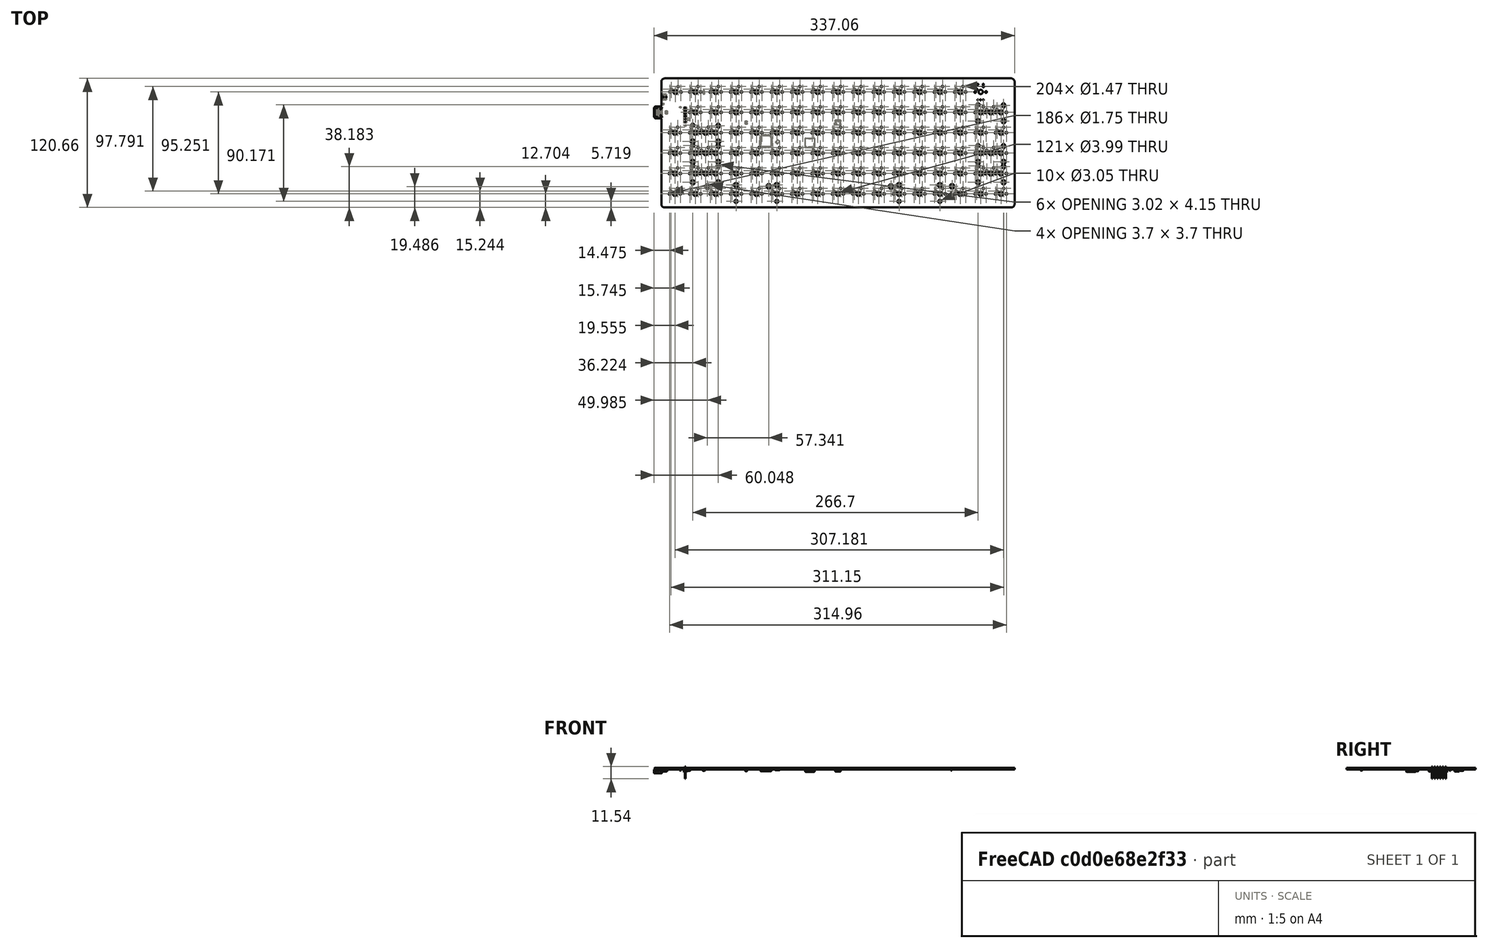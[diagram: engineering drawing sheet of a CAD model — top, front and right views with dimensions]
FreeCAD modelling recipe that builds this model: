
FCSTD DOCUMENT  (FreeCAD 0.19R24291 (Git))
Label: Orthonite87_001
License: All rights reserved
LicenseURL: http://en.wikipedia.org/wiki/All_rights_reserved
objects: App::Link×162, Part::Feature×18, App::Part×4, PartDesign::CoordinateSystem×1, Sketcher::SketchObject×1
note: 20 computed .brp shape members not serialized (recipe doc carries the construction recipe); baked Part::Feature solids carry a one-line shape summary decoded from their .brp

FEATURE [PartDesign::CoordinateSystem] Local_CS_e1db
  AttacherType = Attacher::AttachEngine3D
FEATURE [Part::Feature] Pcb_e1db
  Placement = pos=(-174.625,80.9625,0) rot=(0,0,1;0rad)
  shape: bbox 336.6 x 120.7 x 1.6 mm, 675 faces (baked)
FEATURE [Sketcher::SketchObject] PCB_Sketch_e1db
  FullyConstrained = false
  sketch-geometry (18):
    g0: LineSegment StartX=-168.275 StartY=33.3375 StartZ=0 EndX=-168.275 EndY=23.8125 EndZ=0
    g1: LineSegment StartX=-163.512 StartY=23.0188 StartZ=0 EndX=-162.719 EndY=23.0188 EndZ=0
    g2: LineSegment StartX=-163.512 StartY=34.1313 StartZ=0 EndX=-162.719 EndY=34.1313 EndZ=0
    g3: LineSegment StartX=-167.481 StartY=34.1313 StartZ=0 EndX=-163.512 EndY=34.1313 EndZ=0
    g4: LineSegment StartX=-163.512 StartY=23.0188 StartZ=0 EndX=-167.481 EndY=23.0188 EndZ=0
    g5: LineSegment StartX=-161.925 StartY=22.225 StartZ=0 EndX=-161.925 EndY=-57.15 EndZ=0
    g6: LineSegment StartX=-161.925 StartY=57.15 StartZ=0 EndX=-161.925 EndY=34.925 EndZ=0
    g7: LineSegment StartX=168.275 StartY=-57.15 StartZ=0 EndX=168.275 EndY=57.15 EndZ=0
    g8: LineSegment StartX=-158.75 StartY=-60.325 StartZ=0 EndX=165.1 EndY=-60.325 EndZ=0
    g9: LineSegment StartX=-158.75 StartY=60.325 StartZ=0 EndX=165.1 EndY=60.325 EndZ=0
    g10: ArcOfCircle CenterX=-167.481 CenterY=33.3375 CenterZ=0 NormalX=0 NormalY=0 NormalZ=1 AngleXU=0 Radius=0.79375 StartAngle=1.5708 EndAngle=3.14159
    g11: ArcOfCircle CenterX=-167.481 CenterY=23.8125 CenterZ=0 NormalX=0 NormalY=0 NormalZ=1 AngleXU=0 Radius=0.79375 StartAngle=3.14159 EndAngle=4.71239
    g12: ArcOfCircle CenterX=-162.719 CenterY=22.225 CenterZ=0 NormalX=0 NormalY=0 NormalZ=1 AngleXU=0 Radius=0.79375 StartAngle=0 EndAngle=1.5708
    g13: ArcOfCircle CenterX=-162.719 CenterY=34.925 CenterZ=0 NormalX=0 NormalY=0 NormalZ=1 AngleXU=0 Radius=0.79375 StartAngle=4.71239 EndAngle=6.28319
    g14: ArcOfCircle CenterX=165.1 CenterY=-57.15 CenterZ=0 NormalX=0 NormalY=0 NormalZ=1 AngleXU=0 Radius=3.175 StartAngle=4.71239 EndAngle=6.28319
    g15: ArcOfCircle CenterX=-158.75 CenterY=-57.15 CenterZ=0 NormalX=0 NormalY=0 NormalZ=1 AngleXU=0 Radius=3.175 StartAngle=3.14159 EndAngle=4.71239
    g16: ArcOfCircle CenterX=-158.75 CenterY=57.15 CenterZ=0 NormalX=0 NormalY=0 NormalZ=1 AngleXU=0 Radius=3.175 StartAngle=1.5708 EndAngle=3.14159
    g17: ArcOfCircle CenterX=165.1 CenterY=57.15 CenterZ=0 NormalX=0 NormalY=0 NormalZ=1 AngleXU=0 Radius=3.175 StartAngle=0 EndAngle=1.5708
FEATURE [Part::Feature] Shape  label="C37_C_0603_1608Metric_611CB56A"
  Placement = pos=(109.156,-46.4185,-1.6) rot=(0.707107,0.707107,0;3.14159rad)
  shape: bbox 0.8 x 1.6 x 0.8 mm, 28 faces (baked)
FEATURE [App::Link] C37_C_0603_1608Metric_611CB56A_ln_  label="C36_C_0603_1608Metric_611CB560"
  LinkPlacement = pos=(52.045,-46.6345,-1.6) rot=(0.707107,0.707107,0;3.14159rad)
  LinkedObject = -> Shape
  Placement = pos=(52.045,-46.6345,-1.6) rot=(0.707107,0.707107,0;3.14159rad)
FEATURE [App::Link] C37_C_0603_1608Metric_611CB56A_ln_001  label="C35_C_0603_1608Metric_611CB556"
  LinkPlacement = pos=(-62.166,-46.2285,-1.6) rot=(0.707107,0.707107,0;3.14159rad)
  LinkedObject = -> Shape
  Placement = pos=(-62.166,-46.2285,-1.6) rot=(0.707107,0.707107,0;3.14159rad)
FEATURE [App::Link] C37_C_0603_1608Metric_611CB56A_ln_002  label="C34_C_0603_1608Metric_611CB54C"
  LinkPlacement = pos=(-119.507,-46.5455,-1.6) rot=(0.707107,0.707107,0;3.14159rad)
  LinkedObject = -> Shape
  Placement = pos=(-119.507,-46.5455,-1.6) rot=(0.707107,0.707107,0;3.14159rad)
FEATURE [App::Link] C37_C_0603_1608Metric_611CB56A_ln_003  label="C33_C_0603_1608Metric_611CB542"
  LinkPlacement = pos=(-99.568,-34.3535,-1.6) rot=(1,0,0;3.14159rad)
  LinkedObject = -> Shape
  Placement = pos=(-99.568,-34.3535,-1.6) rot=(1,0,0;3.14159rad)
FEATURE [App::Link] C37_C_0603_1608Metric_611CB56A_ln_004  label="C32_C_0603_1608Metric_611CB538"
  LinkPlacement = pos=(-42.545,-34.3535,-1.6) rot=(1,0,0;3.14159rad)
  LinkedObject = -> Shape
  Placement = pos=(-42.545,-34.3535,-1.6) rot=(1,0,0;3.14159rad)
FEATURE [App::Link] C37_C_0603_1608Metric_611CB56A_ln_005  label="C31_C_0603_1608Metric_611CB52E"
  LinkPlacement = pos=(5.08,-34.3535,-1.6) rot=(1,0,0;3.14159rad)
  LinkedObject = -> Shape
  Placement = pos=(5.08,-34.3535,-1.6) rot=(1,0,0;3.14159rad)
FEATURE [App::Link] C37_C_0603_1608Metric_611CB56A_ln_006  label="C30_C_0603_1608Metric_611CB524"
  LinkPlacement = pos=(71.704,-34.3785,-1.6) rot=(1,0,0;3.14159rad)
  LinkedObject = -> Shape
  Placement = pos=(71.704,-34.3785,-1.6) rot=(1,0,0;3.14159rad)
FEATURE [App::Link] C37_C_0603_1608Metric_611CB56A_ln_007  label="C29_C_0603_1608Metric_611CB51A"
  LinkPlacement = pos=(129.032,-34.3535,-1.6) rot=(1,0,0;3.14159rad)
  LinkedObject = -> Shape
  Placement = pos=(129.032,-34.3535,-1.6) rot=(1,0,0;3.14159rad)
FEATURE [App::Link] C37_C_0603_1608Metric_611CB56A_ln_008  label="C28_C_0603_1608Metric_611CB510"
  LinkPlacement = pos=(128.905,-15.3035,-1.6) rot=(1,0,0;3.14159rad)
  LinkedObject = -> Shape
  Placement = pos=(128.905,-15.3035,-1.6) rot=(1,0,0;3.14159rad)
FEATURE [App::Link] C37_C_0603_1608Metric_611CB56A_ln_009  label="C27_C_0603_1608Metric_611CB506"
  LinkPlacement = pos=(71.882,-15.3035,-1.6) rot=(1,0,0;3.14159rad)
  LinkedObject = -> Shape
  Placement = pos=(71.882,-15.3035,-1.6) rot=(1,0,0;3.14159rad)
FEATURE [App::Link] C37_C_0603_1608Metric_611CB56A_ln_010  label="C26_C_0603_1608Metric_611CB4FC"
  LinkPlacement = pos=(5.08,-15.3035,-1.6) rot=(1,0,0;3.14159rad)
  LinkedObject = -> Shape
  Placement = pos=(5.08,-15.3035,-1.6) rot=(1,0,0;3.14159rad)
FEATURE [App::Link] C37_C_0603_1608Metric_611CB56A_ln_011  label="C25_C_0603_1608Metric_611CB4F2"
  LinkPlacement = pos=(-42.545,-15.3035,-1.6) rot=(1,0,0;3.14159rad)
  LinkedObject = -> Shape
  Placement = pos=(-42.545,-15.3035,-1.6) rot=(1,0,0;3.14159rad)
FEATURE [App::Link] C37_C_0603_1608Metric_611CB56A_ln_012  label="C24_C_0603_1608Metric_611CB4E8"
  LinkPlacement = pos=(-99.695,-15.3035,-1.6) rot=(1,0,0;3.14159rad)
  LinkedObject = -> Shape
  Placement = pos=(-99.695,-15.3035,-1.6) rot=(1,0,0;3.14159rad)
FEATURE [App::Link] C37_C_0603_1608Metric_611CB56A_ln_013  label="C23_C_0603_1608Metric_611CB4DE"
  LinkPlacement = pos=(-99.695,3.7465,-1.6) rot=(1,0,0;3.14159rad)
  LinkedObject = -> Shape
  Placement = pos=(-99.695,3.7465,-1.6) rot=(1,0,0;3.14159rad)
FEATURE [App::Link] C37_C_0603_1608Metric_611CB56A_ln_014  label="C22_C_0603_1608Metric_611CB4D4"
  LinkPlacement = pos=(-42.545,3.7465,-1.6) rot=(1,0,0;3.14159rad)
  LinkedObject = -> Shape
  Placement = pos=(-42.545,3.7465,-1.6) rot=(1,0,0;3.14159rad)
FEATURE [App::Link] C37_C_0603_1608Metric_611CB56A_ln_015  label="C21_C_0603_1608Metric_611CB4CA"
  LinkPlacement = pos=(5.08,3.7465,-1.6) rot=(1,0,0;3.14159rad)
  LinkedObject = -> Shape
  Placement = pos=(5.08,3.7465,-1.6) rot=(1,0,0;3.14159rad)
FEATURE [App::Link] C37_C_0603_1608Metric_611CB56A_ln_016  label="C20_C_0603_1608Metric_611CB4C0"
  LinkPlacement = pos=(71.755,3.7465,-1.6) rot=(1,0,0;3.14159rad)
  LinkedObject = -> Shape
  Placement = pos=(71.755,3.7465,-1.6) rot=(1,0,0;3.14159rad)
FEATURE [App::Link] C37_C_0603_1608Metric_611CB56A_ln_017  label="C19_C_0603_1608Metric_611CB4B6"
  LinkPlacement = pos=(128.778,3.7465,-1.6) rot=(1,0,0;3.14159rad)
  LinkedObject = -> Shape
  Placement = pos=(128.778,3.7465,-1.6) rot=(1,0,0;3.14159rad)
FEATURE [App::Link] C37_C_0603_1608Metric_611CB56A_ln_018  label="C18_C_0603_1608Metric_611CB4AC"
  LinkPlacement = pos=(128.905,22.7965,-1.6) rot=(1,0,0;3.14159rad)
  LinkedObject = -> Shape
  Placement = pos=(128.905,22.7965,-1.6) rot=(1,0,0;3.14159rad)
FEATURE [App::Link] C37_C_0603_1608Metric_611CB56A_ln_019  label="C17_C_0603_1608Metric_611CB4A2"
  LinkPlacement = pos=(71.628,22.7965,-1.6) rot=(1,0,0;3.14159rad)
  LinkedObject = -> Shape
  Placement = pos=(71.628,22.7965,-1.6) rot=(1,0,0;3.14159rad)
FEATURE [App::Link] C37_C_0603_1608Metric_611CB56A_ln_020  label="C16_C_0603_1608Metric_611CB498"
  LinkPlacement = pos=(5.08,22.7965,-1.6) rot=(1,0,0;3.14159rad)
  LinkedObject = -> Shape
  Placement = pos=(5.08,22.7965,-1.6) rot=(1,0,0;3.14159rad)
FEATURE [App::Link] C37_C_0603_1608Metric_611CB56A_ln_021  label="C15_C_0603_1608Metric_611CB48E"
  LinkPlacement = pos=(-42.672,22.7965,-1.6) rot=(1,0,0;3.14159rad)
  LinkedObject = -> Shape
  Placement = pos=(-42.672,22.7965,-1.6) rot=(1,0,0;3.14159rad)
FEATURE [App::Link] C37_C_0603_1608Metric_611CB56A_ln_022  label="C14_C_0603_1608Metric_611CB484"
  LinkPlacement = pos=(-99.695,22.9235,-1.6) rot=(1,0,0;3.14159rad)
  LinkedObject = -> Shape
  Placement = pos=(-99.695,22.9235,-1.6) rot=(1,0,0;3.14159rad)
FEATURE [App::Link] C37_C_0603_1608Metric_611CB56A_ln_023  label="C13_C_0603_1608Metric_611CB47A"
  LinkPlacement = pos=(-139.231,17.7483,-1.6) rot=(0,1,0;3.14159rad)
  LinkedObject = -> Shape
  Placement = pos=(-139.231,17.7483,-1.6) rot=(0,1,0;3.14159rad)
FEATURE [App::Link] C37_C_0603_1608Metric_611CB56A_ln_024  label="C12_C_0603_1608Metric_611CB470"
  LinkPlacement = pos=(-134.144,21.4313,-1.6) rot=(-0.707107,0.707107,0;3.14159rad)
  LinkedObject = -> Shape
  Placement = pos=(-134.144,21.4313,-1.6) rot=(-0.707107,0.707107,0;3.14159rad)
FEATURE [App::Link] C37_C_0603_1608Metric_611CB56A_ln_025  label="C11_C_0603_1608Metric_611CB466"
  LinkPlacement = pos=(-51.054,4.7625,-1.6) rot=(1,0,0;3.14159rad)
  LinkedObject = -> Shape
  Placement = pos=(-51.054,4.7625,-1.6) rot=(1,0,0;3.14159rad)
FEATURE [App::Link] C37_C_0603_1608Metric_611CB56A_ln_026  label="C10_C_0603_1608Metric_611CB45C"
  LinkPlacement = pos=(-50.165,-1.0795,-1.6) rot=(1,0,0;3.14159rad)
  LinkedObject = -> Shape
  Placement = pos=(-50.165,-1.0795,-1.6) rot=(1,0,0;3.14159rad)
FEATURE [App::Link] C37_C_0603_1608Metric_611CB56A_ln_027  label="C9_C_0603_1608Metric_611CB452"
  LinkPlacement = pos=(-79.375,19.05,-1.6) rot=(-0.707107,0.707107,0;3.14159rad)
  LinkedObject = -> Shape
  Placement = pos=(-79.375,19.05,-1.6) rot=(-0.707107,0.707107,0;3.14159rad)
FEATURE [App::Link] C37_C_0603_1608Metric_611CB56A_ln_028  label="C8_C_0603_1608Metric_611CB448"
  LinkPlacement = pos=(-85.725,19.05,-1.6) rot=(-0.707107,0.707107,0;3.14159rad)
  LinkedObject = -> Shape
  Placement = pos=(-85.725,19.05,-1.6) rot=(-0.707107,0.707107,0;3.14159rad)
FEATURE [App::Link] C37_C_0603_1608Metric_611CB56A_ln_029  label="C7_C_0603_1608Metric_611CB43E"
  LinkPlacement = pos=(-146.844,34.1313,-1.6) rot=(-0.707107,0.707107,0;3.14159rad)
  LinkedObject = -> Shape
  Placement = pos=(-146.844,34.1313,-1.6) rot=(-0.707107,0.707107,0;3.14159rad)
FEATURE [App::Link] C37_C_0603_1608Metric_611CB56A_ln_030  label="C6_C_0603_1608Metric_611CB434"
  LinkPlacement = pos=(-61.722,-8.1915,-1.6) rot=(0.707107,0.707107,0;3.14159rad)
  LinkedObject = -> Shape
  Placement = pos=(-61.722,-8.1915,-1.6) rot=(0.707107,0.707107,0;3.14159rad)
FEATURE [App::Link] C37_C_0603_1608Metric_611CB56A_ln_031  label="C5_C_0603_1608Metric_611CB42A"
  LinkPlacement = pos=(-55.88,-3.6195,-1.6) rot=(0.707107,0.707107,0;3.14159rad)
  LinkedObject = -> Shape
  Placement = pos=(-55.88,-3.6195,-1.6) rot=(0.707107,0.707107,0;3.14159rad)
FEATURE [App::Link] C37_C_0603_1608Metric_611CB56A_ln_032  label="C4_C_0603_1608Metric_611CB420"
  LinkPlacement = pos=(-65.532,-8.0645,-1.6) rot=(0.707107,0.707107,0;3.14159rad)
  LinkedObject = -> Shape
  Placement = pos=(-65.532,-8.0645,-1.6) rot=(0.707107,0.707107,0;3.14159rad)
FEATURE [App::Link] C37_C_0603_1608Metric_611CB56A_ln_033  label="C3_C_0603_1608Metric_611CB416"
  LinkPlacement = pos=(-73.279,5.0165,-1.6) rot=(1,0,0;3.14159rad)
  LinkedObject = -> Shape
  Placement = pos=(-73.279,5.0165,-1.6) rot=(1,0,0;3.14159rad)
FEATURE [App::Link] C37_C_0603_1608Metric_611CB56A_ln_034  label="C2_C_0603_1608Metric_611CB40C"
  LinkPlacement = pos=(-62.23,10.8585,-1.6) rot=(-0.707107,0.707107,0;3.14159rad)
  LinkedObject = -> Shape
  Placement = pos=(-62.23,10.8585,-1.6) rot=(-0.707107,0.707107,0;3.14159rad)
FEATURE [App::Link] C37_C_0603_1608Metric_611CB56A_ln_035  label="C1_C_0603_1608Metric_611CB402"
  LinkPlacement = pos=(-75.819,4.1275,-1.6) rot=(-0.707107,0.707107,0;3.14159rad)
  LinkedObject = -> Shape
  Placement = pos=(-75.819,4.1275,-1.6) rot=(-0.707107,0.707107,0;3.14159rad)
FEATURE [Part::Feature] Shape001  label="D_2_D_SOD_123_611CB7E4"
  Placement = pos=(-122.174,47.3075,-1.6) rot=(0.707107,0.707107,0;3.14159rad)
  shape: bbox 1.6 x 3.8 x 1.25 mm, 67 faces (baked)
FEATURE [App::Link] D_2_D_SOD_123_611CB7E4_ln_  label="D_1_2_D_SOD_123_611CB7D3"
  LinkPlacement = pos=(-141.224,47.3085,-1.6) rot=(0.707107,0.707107,0;3.14159rad)
  LinkedObject = -> Shape001
  Placement = pos=(-141.224,47.3085,-1.6) rot=(0.707107,0.707107,0;3.14159rad)
FEATURE [App::Link] D_2_D_SOD_123_611CB7E4_ln_001  label="D_100_2_D_SOD_123_611CBE66"
  LinkPlacement = pos=(147.637,-47.2435,-1.6) rot=(0.707107,0.707107,0;3.14159rad)
  LinkedObject = -> Shape001
  Placement = pos=(147.637,-47.2435,-1.6) rot=(0.707107,0.707107,0;3.14159rad)
FEATURE [App::Link] D_2_D_SOD_123_611CB7E4_ln_002  label="D_99_2_D_SOD_123_611CBE55"
  LinkPlacement = pos=(144.463,-47.2435,-1.6) rot=(0.707107,0.707107,0;3.14159rad)
  LinkedObject = -> Shape001
  Placement = pos=(144.463,-47.2435,-1.6) rot=(0.707107,0.707107,0;3.14159rad)
FEATURE [App::Link] D_2_D_SOD_123_611CB7E4_ln_003  label="D_98_2_D_SOD_123_611CBE44"
  LinkPlacement = pos=(125.476,-47.2435,-1.6) rot=(0.707107,0.707107,0;3.14159rad)
  LinkedObject = -> Shape001
  Placement = pos=(125.476,-47.2435,-1.6) rot=(0.707107,0.707107,0;3.14159rad)
FEATURE [App::Link] D_2_D_SOD_123_611CB7E4_ln_004  label="D_97_2_D_SOD_123_611CBE33"
  LinkPlacement = pos=(106.363,-47.2435,-1.6) rot=(0.707107,0.707107,0;3.14159rad)
  LinkedObject = -> Shape001
  Placement = pos=(106.363,-47.2435,-1.6) rot=(0.707107,0.707107,0;3.14159rad)
FEATURE [App::Link] D_2_D_SOD_123_611CB7E4_ln_005  label="D_96_2_D_SOD_123_611CBE22"
  LinkPlacement = pos=(87.313,-47.2435,-1.6) rot=(0.707107,0.707107,0;3.14159rad)
  LinkedObject = -> Shape001
  Placement = pos=(87.313,-47.2435,-1.6) rot=(0.707107,0.707107,0;3.14159rad)
FEATURE [App::Link] D_2_D_SOD_123_611CB7E4_ln_006  label="D_95_2_D_SOD_123_611CBE11"
  LinkPlacement = pos=(68.326,-47.2435,-1.6) rot=(0.707107,0.707107,0;3.14159rad)
  LinkedObject = -> Shape001
  Placement = pos=(68.326,-47.2435,-1.6) rot=(0.707107,0.707107,0;3.14159rad)
FEATURE [App::Link] D_2_D_SOD_123_611CB7E4_ln_007  label="D_94_2_D_SOD_123_611CBE00"
  LinkPlacement = pos=(49.213,-47.2435,-1.6) rot=(0.707107,0.707107,0;3.14159rad)
  LinkedObject = -> Shape001
  Placement = pos=(49.213,-47.2435,-1.6) rot=(0.707107,0.707107,0;3.14159rad)
FEATURE [App::Link] D_2_D_SOD_123_611CB7E4_ln_008  label="D_93_2_D_SOD_123_611CBDEF"
  LinkPlacement = pos=(30.163,-47.2435,-1.6) rot=(0.707107,0.707107,0;3.14159rad)
  LinkedObject = -> Shape001
  Placement = pos=(30.163,-47.2435,-1.6) rot=(0.707107,0.707107,0;3.14159rad)
FEATURE [App::Link] D_2_D_SOD_123_611CB7E4_ln_009  label="D_92_2_D_SOD_123_611CBDDE"
  LinkPlacement = pos=(11.176,-47.2435,-1.6) rot=(0.707107,0.707107,0;3.14159rad)
  LinkedObject = -> Shape001
  Placement = pos=(11.176,-47.2435,-1.6) rot=(0.707107,0.707107,0;3.14159rad)
FEATURE [App::Link] D_2_D_SOD_123_611CB7E4_ln_010  label="D_91_2_D_SOD_123_611CBDCD"
  LinkPlacement = pos=(-7.874,-47.2435,-1.6) rot=(0.707107,0.707107,0;3.14159rad)
  LinkedObject = -> Shape001
  Placement = pos=(-7.874,-47.2435,-1.6) rot=(0.707107,0.707107,0;3.14159rad)
FEATURE [App::Link] D_2_D_SOD_123_611CB7E4_ln_011  label="D_90_2_D_SOD_123_611CBDBC"
  LinkPlacement = pos=(-26.987,-47.3075,-1.6) rot=(0.707107,0.707107,0;3.14159rad)
  LinkedObject = -> Shape001
  Placement = pos=(-26.987,-47.3075,-1.6) rot=(0.707107,0.707107,0;3.14159rad)
FEATURE [App::Link] D_2_D_SOD_123_611CB7E4_ln_012  label="D_89_2_D_SOD_123_611CBDAB"
  LinkPlacement = pos=(-46.037,-47.2435,-1.6) rot=(0.707107,0.707107,0;3.14159rad)
  LinkedObject = -> Shape001
  Placement = pos=(-46.037,-47.2435,-1.6) rot=(0.707107,0.707107,0;3.14159rad)
FEATURE [App::Link] D_2_D_SOD_123_611CB7E4_ln_013  label="D_88_2_D_SOD_123_611CBD9A"
  LinkPlacement = pos=(-65.087,-47.2435,-1.6) rot=(0.707107,0.707107,0;3.14159rad)
  LinkedObject = -> Shape001
  Placement = pos=(-65.087,-47.2435,-1.6) rot=(0.707107,0.707107,0;3.14159rad)
FEATURE [App::Link] D_2_D_SOD_123_611CB7E4_ln_014  label="D_87_2_D_SOD_123_611CBD89"
  LinkPlacement = pos=(-84.1375,-47.3075,-1.6) rot=(0.707107,0.707107,0;3.14159rad)
  LinkedObject = -> Shape001
  Placement = pos=(-84.1375,-47.3075,-1.6) rot=(0.707107,0.707107,0;3.14159rad)
FEATURE [App::Link] D_2_D_SOD_123_611CB7E4_ln_015  label="D_86_2_D_SOD_123_611CBD78"
  LinkPlacement = pos=(-103.187,-47.2435,-1.6) rot=(0.707107,0.707107,0;3.14159rad)
  LinkedObject = -> Shape001
  Placement = pos=(-103.187,-47.2435,-1.6) rot=(0.707107,0.707107,0;3.14159rad)
FEATURE [App::Link] D_2_D_SOD_123_611CB7E4_ln_016  label="D_85_2_D_SOD_123_611CBD67"
  LinkPlacement = pos=(-122.237,-47.3075,-1.6) rot=(0.707107,0.707107,0;3.14159rad)
  LinkedObject = -> Shape001
  Placement = pos=(-122.237,-47.3075,-1.6) rot=(0.707107,0.707107,0;3.14159rad)
FEATURE [App::Link] D_2_D_SOD_123_611CB7E4_ln_017  label="D_84_2_D_SOD_123_611CBD56"
  LinkPlacement = pos=(-141.288,-47.3075,-1.6) rot=(0.707107,0.707107,0;3.14159rad)
  LinkedObject = -> Shape001
  Placement = pos=(-141.288,-47.3075,-1.6) rot=(0.707107,0.707107,0;3.14159rad)
FEATURE [App::Link] D_2_D_SOD_123_611CB7E4_ln_018  label="D_83_2_D_SOD_123_611CBD45"
  LinkPlacement = pos=(144.463,-21.4635,-1.6) rot=(0.707107,0.707107,0;3.14159rad)
  LinkedObject = -> Shape001
  Placement = pos=(144.463,-21.4635,-1.6) rot=(0.707107,0.707107,0;3.14159rad)
FEATURE [App::Link] D_2_D_SOD_123_611CB7E4_ln_019  label="D_82_2_D_SOD_123_611CBD34"
  LinkPlacement = pos=(128.587,-28.2575,-1.6) rot=(0.707107,0.707107,0;3.14159rad)
  LinkedObject = -> Shape001
  Placement = pos=(128.587,-28.2575,-1.6) rot=(0.707107,0.707107,0;3.14159rad)
FEATURE [App::Link] D_2_D_SOD_123_611CB7E4_ln_020  label="D_81_2_D_SOD_123_611CBD23"
  LinkPlacement = pos=(125.413,-28.2575,-1.6) rot=(0.707107,0.707107,0;3.14159rad)
  LinkedObject = -> Shape001
  Placement = pos=(125.413,-28.2575,-1.6) rot=(0.707107,0.707107,0;3.14159rad)
FEATURE [App::Link] D_2_D_SOD_123_611CB7E4_ln_021  label="D_80_2_D_SOD_123_611CBD12"
  LinkPlacement = pos=(106.363,-28.1935,-1.6) rot=(0.707107,0.707107,0;3.14159rad)
  LinkedObject = -> Shape001
  Placement = pos=(106.363,-28.1935,-1.6) rot=(0.707107,0.707107,0;3.14159rad)
FEATURE [App::Link] D_2_D_SOD_123_611CB7E4_ln_022  label="D_79_2_D_SOD_123_611CBD01"
  LinkPlacement = pos=(87.313,-28.1935,-1.6) rot=(0.707107,0.707107,0;3.14159rad)
  LinkedObject = -> Shape001
  Placement = pos=(87.313,-28.1935,-1.6) rot=(0.707107,0.707107,0;3.14159rad)
FEATURE [App::Link] D_2_D_SOD_123_611CB7E4_ln_023  label="D_78_2_D_SOD_123_611CBCF0"
  LinkPlacement = pos=(68.263,-28.1935,-1.6) rot=(0.707107,0.707107,0;3.14159rad)
  LinkedObject = -> Shape001
  Placement = pos=(68.263,-28.1935,-1.6) rot=(0.707107,0.707107,0;3.14159rad)
FEATURE [App::Link] D_2_D_SOD_123_611CB7E4_ln_024  label="D_77_2_D_SOD_123_611CBCDF"
  LinkPlacement = pos=(49.213,-28.1935,-1.6) rot=(0.707107,0.707107,0;3.14159rad)
  LinkedObject = -> Shape001
  Placement = pos=(49.213,-28.1935,-1.6) rot=(0.707107,0.707107,0;3.14159rad)
FEATURE [App::Link] D_2_D_SOD_123_611CB7E4_ln_025  label="D_76_2_D_SOD_123_611CBCCE"
  LinkPlacement = pos=(30.163,-28.1935,-1.6) rot=(0.707107,0.707107,0;3.14159rad)
  LinkedObject = -> Shape001
  Placement = pos=(30.163,-28.1935,-1.6) rot=(0.707107,0.707107,0;3.14159rad)
FEATURE [App::Link] D_2_D_SOD_123_611CB7E4_ln_026  label="D_75_2_D_SOD_123_611CBCBD"
  LinkPlacement = pos=(11.113,-28.1935,-1.6) rot=(0.707107,0.707107,0;3.14159rad)
  LinkedObject = -> Shape001
  Placement = pos=(11.113,-28.1935,-1.6) rot=(0.707107,0.707107,0;3.14159rad)
FEATURE [App::Link] D_2_D_SOD_123_611CB7E4_ln_027  label="D_74_2_D_SOD_123_611CBCAC"
  LinkPlacement = pos=(-7.937,-28.1935,-1.6) rot=(0.707107,0.707107,0;3.14159rad)
  LinkedObject = -> Shape001
  Placement = pos=(-7.937,-28.1935,-1.6) rot=(0.707107,0.707107,0;3.14159rad)
FEATURE [App::Link] D_2_D_SOD_123_611CB7E4_ln_028  label="D_73_2_D_SOD_123_611CBC9B"
  LinkPlacement = pos=(-26.987,-28.1935,-1.6) rot=(0.707107,0.707107,0;3.14159rad)
  LinkedObject = -> Shape001
  Placement = pos=(-26.987,-28.1935,-1.6) rot=(0.707107,0.707107,0;3.14159rad)
FEATURE [App::Link] D_2_D_SOD_123_611CB7E4_ln_029  label="D_72_2_D_SOD_123_611CBC8A"
  LinkPlacement = pos=(-46.037,-28.1935,-1.6) rot=(0.707107,0.707107,0;3.14159rad)
  LinkedObject = -> Shape001
  Placement = pos=(-46.037,-28.1935,-1.6) rot=(0.707107,0.707107,0;3.14159rad)
FEATURE [App::Link] D_2_D_SOD_123_611CB7E4_ln_030  label="D_71_2_D_SOD_123_611CBC79"
  LinkPlacement = pos=(-65.087,-28.1935,-1.6) rot=(0.707107,0.707107,0;3.14159rad)
  LinkedObject = -> Shape001
  Placement = pos=(-65.087,-28.1935,-1.6) rot=(0.707107,0.707107,0;3.14159rad)
FEATURE [App::Link] D_2_D_SOD_123_611CB7E4_ln_031  label="D_70_2_D_SOD_123_611CBC68"
  LinkPlacement = pos=(-84.1375,-28.1935,-1.6) rot=(0.707107,0.707107,0;3.14159rad)
  LinkedObject = -> Shape001
  Placement = pos=(-84.1375,-28.1935,-1.6) rot=(0.707107,0.707107,0;3.14159rad)
FEATURE [App::Link] D_2_D_SOD_123_611CB7E4_ln_032  label="D_69_2_D_SOD_123_611CBC57"
  LinkPlacement = pos=(-103.124,-28.1935,-1.6) rot=(0.707107,0.707107,0;3.14159rad)
  LinkedObject = -> Shape001
  Placement = pos=(-103.124,-28.1935,-1.6) rot=(0.707107,0.707107,0;3.14159rad)
FEATURE [App::Link] D_2_D_SOD_123_611CB7E4_ln_033  label="D_68_2_D_SOD_123_611CBC46"
  LinkPlacement = pos=(-122.174,-21.3995,-1.6) rot=(0.707107,0.707107,0;3.14159rad)
  LinkedObject = -> Shape001
  Placement = pos=(-122.174,-21.3995,-1.6) rot=(0.707107,0.707107,0;3.14159rad)
FEATURE [App::Link] D_2_D_SOD_123_611CB7E4_ln_034  label="D_67_2_D_SOD_123_611CBC35"
  LinkPlacement = pos=(-141.287,-28.1935,-1.6) rot=(0.707107,0.707107,0;3.14159rad)
  LinkedObject = -> Shape001
  Placement = pos=(-141.287,-28.1935,-1.6) rot=(0.707107,0.707107,0;3.14159rad)
FEATURE [App::Link] D_2_D_SOD_123_611CB7E4_ln_035  label="D_66_2_D_SOD_123_611CBC24"
  LinkPlacement = pos=(144.589,-2.3495,-1.6) rot=(0.707107,0.707107,0;3.14159rad)
  LinkedObject = -> Shape001
  Placement = pos=(144.589,-2.3495,-1.6) rot=(0.707107,0.707107,0;3.14159rad)
FEATURE [App::Link] D_2_D_SOD_123_611CB7E4_ln_036  label="D_65_2_D_SOD_123_611CBC13"
  LinkPlacement = pos=(128.524,-9.144,-1.6) rot=(0.707107,0.707107,0;3.14159rad)
  LinkedObject = -> Shape001
  Placement = pos=(128.524,-9.144,-1.6) rot=(0.707107,0.707107,0;3.14159rad)
FEATURE [App::Link] D_2_D_SOD_123_611CB7E4_ln_037  label="D_64_2_D_SOD_123_611CBC02"
  LinkPlacement = pos=(125.476,-9.144,-1.6) rot=(0.707107,0.707107,0;3.14159rad)
  LinkedObject = -> Shape001
  Placement = pos=(125.476,-9.144,-1.6) rot=(0.707107,0.707107,0;3.14159rad)
FEATURE [App::Link] D_2_D_SOD_123_611CB7E4_ln_038  label="D_63_2_D_SOD_123_611CBBF1"
  LinkPlacement = pos=(106.426,-9.144,-1.6) rot=(0.707107,0.707107,0;3.14159rad)
  LinkedObject = -> Shape001
  Placement = pos=(106.426,-9.144,-1.6) rot=(0.707107,0.707107,0;3.14159rad)
FEATURE [App::Link] D_2_D_SOD_123_611CB7E4_ln_039  label="D_62_2_D_SOD_123_611CBBE0"
  LinkPlacement = pos=(87.376,-9.144,-1.6) rot=(0.707107,0.707107,0;3.14159rad)
  LinkedObject = -> Shape001
  Placement = pos=(87.376,-9.144,-1.6) rot=(0.707107,0.707107,0;3.14159rad)
FEATURE [App::Link] D_2_D_SOD_123_611CB7E4_ln_040  label="D_61_2_D_SOD_123_611CBBCF"
  LinkPlacement = pos=(68.263,-9.144,-1.6) rot=(0.707107,0.707107,0;3.14159rad)
  LinkedObject = -> Shape001
  Placement = pos=(68.263,-9.144,-1.6) rot=(0.707107,0.707107,0;3.14159rad)
FEATURE [App::Link] D_2_D_SOD_123_611CB7E4_ln_041  label="D_60_2_D_SOD_123_611CBBBE"
  LinkPlacement = pos=(49.276,-9.144,-1.6) rot=(0.707107,0.707107,0;3.14159rad)
  LinkedObject = -> Shape001
  Placement = pos=(49.276,-9.144,-1.6) rot=(0.707107,0.707107,0;3.14159rad)
FEATURE [App::Link] D_2_D_SOD_123_611CB7E4_ln_042  label="D_59_2_D_SOD_123_611CBBAD"
  LinkPlacement = pos=(30.226,-9.144,-1.6) rot=(0.707107,0.707107,0;3.14159rad)
  LinkedObject = -> Shape001
  Placement = pos=(30.226,-9.144,-1.6) rot=(0.707107,0.707107,0;3.14159rad)
FEATURE [App::Link] D_2_D_SOD_123_611CB7E4_ln_043  label="D_58_2_D_SOD_123_611CBB9C"
  LinkPlacement = pos=(11.176,-9.2075,-1.6) rot=(0.707107,0.707107,0;3.14159rad)
  LinkedObject = -> Shape001
  Placement = pos=(11.176,-9.2075,-1.6) rot=(0.707107,0.707107,0;3.14159rad)
FEATURE [App::Link] D_2_D_SOD_123_611CB7E4_ln_044  label="D_57_2_D_SOD_123_611CBB8B"
  LinkPlacement = pos=(-7.874,-9.144,-1.6) rot=(0.707107,0.707107,0;3.14159rad)
  LinkedObject = -> Shape001
  Placement = pos=(-7.874,-9.144,-1.6) rot=(0.707107,0.707107,0;3.14159rad)
FEATURE [App::Link] D_2_D_SOD_123_611CB7E4_ln_045  label="D_56_2_D_SOD_123_611CBB7A"
  LinkPlacement = pos=(-26.924,-9.144,-1.6) rot=(0.707107,0.707107,0;3.14159rad)
  LinkedObject = -> Shape001
  Placement = pos=(-26.924,-9.144,-1.6) rot=(0.707107,0.707107,0;3.14159rad)
FEATURE [App::Link] D_2_D_SOD_123_611CB7E4_ln_046  label="D_55_2_D_SOD_123_611CBB69"
  LinkPlacement = pos=(-45.974,-9.144,-1.6) rot=(0.707107,0.707107,0;3.14159rad)
  LinkedObject = -> Shape001
  Placement = pos=(-45.974,-9.144,-1.6) rot=(0.707107,0.707107,0;3.14159rad)
FEATURE [App::Link] D_2_D_SOD_123_611CB7E4_ln_047  label="D_54_2_D_SOD_123_611CBB58"
  LinkPlacement = pos=(-80.899,-9.144,-1.6) rot=(0.707107,0.707107,0;3.14159rad)
  LinkedObject = -> Shape001
  Placement = pos=(-80.899,-9.144,-1.6) rot=(0.707107,0.707107,0;3.14159rad)
FEATURE [App::Link] D_2_D_SOD_123_611CB7E4_ln_048  label="D_53_2_D_SOD_123_611CBB47"
  LinkPlacement = pos=(-84.074,-9.144,-1.6) rot=(0.707107,0.707107,0;3.14159rad)
  LinkedObject = -> Shape001
  Placement = pos=(-84.074,-9.144,-1.6) rot=(0.707107,0.707107,0;3.14159rad)
FEATURE [App::Link] D_2_D_SOD_123_611CB7E4_ln_049  label="D_52_2_D_SOD_123_611CBB36"
  LinkPlacement = pos=(-103.124,-8.509,-1.6) rot=(0.707107,0.707107,0;3.14159rad)
  LinkedObject = -> Shape001
  Placement = pos=(-103.124,-8.509,-1.6) rot=(0.707107,0.707107,0;3.14159rad)
FEATURE [App::Link] D_2_D_SOD_123_611CB7E4_ln_050  label="D_51_2_D_SOD_123_611CBB25"
  LinkPlacement = pos=(-122.174,-2.413,-1.6) rot=(0.707107,0.707107,0;3.14159rad)
  LinkedObject = -> Shape001
  Placement = pos=(-122.174,-2.413,-1.6) rot=(0.707107,0.707107,0;3.14159rad)
FEATURE [App::Link] D_2_D_SOD_123_611CB7E4_ln_051  label="D_50_2_D_SOD_123_611CBB14"
  LinkPlacement = pos=(-141.224,-9.144,-1.6) rot=(0.707107,0.707107,0;3.14159rad)
  LinkedObject = -> Shape001
  Placement = pos=(-141.224,-9.144,-1.6) rot=(0.707107,0.707107,0;3.14159rad)
FEATURE [App::Link] D_2_D_SOD_123_611CB7E4_ln_052  label="D_49_2_D_SOD_123_611CBB03"
  LinkPlacement = pos=(147.574,9.906,-1.6) rot=(0.707107,0.707107,0;3.14159rad)
  LinkedObject = -> Shape001
  Placement = pos=(147.574,9.906,-1.6) rot=(0.707107,0.707107,0;3.14159rad)
FEATURE [App::Link] D_2_D_SOD_123_611CB7E4_ln_053  label="D_48_2_D_SOD_123_611CBAF2"
  LinkPlacement = pos=(144.526,9.906,-1.6) rot=(0.707107,0.707107,0;3.14159rad)
  LinkedObject = -> Shape001
  Placement = pos=(144.526,9.906,-1.6) rot=(0.707107,0.707107,0;3.14159rad)
FEATURE [App::Link] D_2_D_SOD_123_611CB7E4_ln_054  label="D_47_2_D_SOD_123_611CBAE1"
  LinkPlacement = pos=(125.476,9.906,-1.6) rot=(0.707107,0.707107,0;3.14159rad)
  LinkedObject = -> Shape001
  Placement = pos=(125.476,9.906,-1.6) rot=(0.707107,0.707107,0;3.14159rad)
FEATURE [App::Link] D_2_D_SOD_123_611CB7E4_ln_055  label="D_46_2_D_SOD_123_611CBAD0"
  LinkPlacement = pos=(106.426,9.906,-1.6) rot=(0.707107,0.707107,0;3.14159rad)
  LinkedObject = -> Shape001
  Placement = pos=(106.426,9.906,-1.6) rot=(0.707107,0.707107,0;3.14159rad)
FEATURE [App::Link] D_2_D_SOD_123_611CB7E4_ln_056  label="D_45_2_D_SOD_123_611CBABF"
  LinkPlacement = pos=(87.376,9.906,-1.6) rot=(0.707107,0.707107,0;3.14159rad)
  LinkedObject = -> Shape001
  Placement = pos=(87.376,9.906,-1.6) rot=(0.707107,0.707107,0;3.14159rad)
FEATURE [App::Link] D_2_D_SOD_123_611CB7E4_ln_057  label="D_44_2_D_SOD_123_611CBAAE"
  LinkPlacement = pos=(68.326,9.906,-1.6) rot=(0.707107,0.707107,0;3.14159rad)
  LinkedObject = -> Shape001
  Placement = pos=(68.326,9.906,-1.6) rot=(0.707107,0.707107,0;3.14159rad)
FEATURE [App::Link] D_2_D_SOD_123_611CB7E4_ln_058  label="D_43_2_D_SOD_123_611CBA9D"
  LinkPlacement = pos=(49.276,9.906,-1.6) rot=(0.707107,0.707107,0;3.14159rad)
  LinkedObject = -> Shape001
  Placement = pos=(49.276,9.906,-1.6) rot=(0.707107,0.707107,0;3.14159rad)
FEATURE [App::Link] D_2_D_SOD_123_611CB7E4_ln_059  label="D_42_2_D_SOD_123_611CBA8C"
  LinkPlacement = pos=(30.226,9.906,-1.6) rot=(0.707107,0.707107,0;3.14159rad)
  LinkedObject = -> Shape001
  Placement = pos=(30.226,9.906,-1.6) rot=(0.707107,0.707107,0;3.14159rad)
FEATURE [App::Link] D_2_D_SOD_123_611CB7E4_ln_060  label="D_41_2_D_SOD_123_611CBA7B"
  LinkPlacement = pos=(11.176,9.906,-1.6) rot=(0.707107,0.707107,0;3.14159rad)
  LinkedObject = -> Shape001
  Placement = pos=(11.176,9.906,-1.6) rot=(0.707107,0.707107,0;3.14159rad)
FEATURE [App::Link] D_2_D_SOD_123_611CB7E4_ln_061  label="D_40_2_D_SOD_123_611CBA6A"
  LinkPlacement = pos=(-7.874,9.906,-1.6) rot=(0.707107,0.707107,0;3.14159rad)
  LinkedObject = -> Shape001
  Placement = pos=(-7.874,9.906,-1.6) rot=(0.707107,0.707107,0;3.14159rad)
FEATURE [App::Link] D_2_D_SOD_123_611CB7E4_ln_062  label="D_39_2_D_SOD_123_611CBA59"
  LinkPlacement = pos=(-26.924,9.906,-1.6) rot=(0.707107,0.707107,0;3.14159rad)
  LinkedObject = -> Shape001
  Placement = pos=(-26.924,9.906,-1.6) rot=(0.707107,0.707107,0;3.14159rad)
FEATURE [App::Link] D_2_D_SOD_123_611CB7E4_ln_063  label="D_38_2_D_SOD_123_611CBA48"
  LinkPlacement = pos=(-45.974,9.906,-1.6) rot=(0.707107,0.707107,0;3.14159rad)
  LinkedObject = -> Shape001
  Placement = pos=(-45.974,9.906,-1.6) rot=(0.707107,0.707107,0;3.14159rad)
FEATURE [App::Link] D_2_D_SOD_123_611CB7E4_ln_064  label="D_37_2_D_SOD_123_611CBA37"
  LinkPlacement = pos=(-80.899,9.906,-1.6) rot=(0.707107,0.707107,0;3.14159rad)
  LinkedObject = -> Shape001
  Placement = pos=(-80.899,9.906,-1.6) rot=(0.707107,0.707107,0;3.14159rad)
FEATURE [App::Link] D_2_D_SOD_123_611CB7E4_ln_065  label="D_36_2_D_SOD_123_611CBA26"
  LinkPlacement = pos=(-84.074,9.906,-1.6) rot=(0.707107,0.707107,0;3.14159rad)
  LinkedObject = -> Shape001
  Placement = pos=(-84.074,9.906,-1.6) rot=(0.707107,0.707107,0;3.14159rad)
FEATURE [App::Link] D_2_D_SOD_123_611CB7E4_ln_066  label="D_35_2_D_SOD_123_611CBA15"
  LinkPlacement = pos=(-103.124,9.906,-1.6) rot=(0.707107,0.707107,0;3.14159rad)
  LinkedObject = -> Shape001
  Placement = pos=(-103.124,9.906,-1.6) rot=(0.707107,0.707107,0;3.14159rad)
FEATURE [App::Link] D_2_D_SOD_123_611CB7E4_ln_067  label="D_34_2_D_SOD_123_611CBA04"
  LinkPlacement = pos=(-122.174,16.7005,-1.6) rot=(0.707107,0.707107,0;3.14159rad)
  LinkedObject = -> Shape001
  Placement = pos=(-122.174,16.7005,-1.6) rot=(0.707107,0.707107,0;3.14159rad)
FEATURE [App::Link] D_2_D_SOD_123_611CB7E4_ln_068  label="D_33_2_D_SOD_123_611CB9F3"
  LinkPlacement = pos=(-141.224,9.906,-1.6) rot=(0.707107,0.707107,0;3.14159rad)
  LinkedObject = -> Shape001
  Placement = pos=(-141.224,9.906,-1.6) rot=(0.707107,0.707107,0;3.14159rad)
FEATURE [App::Link] D_2_D_SOD_123_611CB7E4_ln_069  label="D_32_2_D_SOD_123_611CB9E2"
  LinkPlacement = pos=(144.526,35.7505,-1.6) rot=(0.707107,0.707107,0;3.14159rad)
  LinkedObject = -> Shape001
  Placement = pos=(144.526,35.7505,-1.6) rot=(0.707107,0.707107,0;3.14159rad)
FEATURE [App::Link] D_2_D_SOD_123_611CB7E4_ln_070  label="D_31_2_D_SOD_123_611CB9D1"
  LinkPlacement = pos=(128.524,28.321,-1.6) rot=(0.707107,0.707107,0;3.14159rad)
  LinkedObject = -> Shape001
  Placement = pos=(128.524,28.321,-1.6) rot=(0.707107,0.707107,0;3.14159rad)
FEATURE [App::Link] D_2_D_SOD_123_611CB7E4_ln_071  label="D_30_2_D_SOD_123_611CB9C0"
  LinkPlacement = pos=(125.476,28.321,-1.6) rot=(0.707107,0.707107,0;3.14159rad)
  LinkedObject = -> Shape001
  Placement = pos=(125.476,28.321,-1.6) rot=(0.707107,0.707107,0;3.14159rad)
FEATURE [App::Link] D_2_D_SOD_123_611CB7E4_ln_072  label="D_29_2_D_SOD_123_611CB9AF"
  LinkPlacement = pos=(106.426,28.321,-1.6) rot=(0.707107,0.707107,0;3.14159rad)
  LinkedObject = -> Shape001
  Placement = pos=(106.426,28.321,-1.6) rot=(0.707107,0.707107,0;3.14159rad)
FEATURE [App::Link] D_2_D_SOD_123_611CB7E4_ln_073  label="D_28_2_D_SOD_123_611CB99E"
  LinkPlacement = pos=(87.376,28.321,-1.6) rot=(0.707107,0.707107,0;3.14159rad)
  LinkedObject = -> Shape001
  Placement = pos=(87.376,28.321,-1.6) rot=(0.707107,0.707107,0;3.14159rad)
FEATURE [App::Link] D_2_D_SOD_123_611CB7E4_ln_074  label="D_27_2_D_SOD_123_611CB98D"
  LinkPlacement = pos=(68.326,28.2575,-1.6) rot=(0.707107,0.707107,0;3.14159rad)
  LinkedObject = -> Shape001
  Placement = pos=(68.326,28.2575,-1.6) rot=(0.707107,0.707107,0;3.14159rad)
FEATURE [App::Link] D_2_D_SOD_123_611CB7E4_ln_075  label="D_26_2_D_SOD_123_611CB97C"
  LinkPlacement = pos=(49.276,28.321,-1.6) rot=(0.707107,0.707107,0;3.14159rad)
  LinkedObject = -> Shape001
  Placement = pos=(49.276,28.321,-1.6) rot=(0.707107,0.707107,0;3.14159rad)
FEATURE [App::Link] D_2_D_SOD_123_611CB7E4_ln_076  label="D_25_2_D_SOD_123_611CB96B"
  LinkPlacement = pos=(30.226,28.2575,-1.6) rot=(0.707107,0.707107,0;3.14159rad)
  LinkedObject = -> Shape001
  Placement = pos=(30.226,28.2575,-1.6) rot=(0.707107,0.707107,0;3.14159rad)
FEATURE [App::Link] D_2_D_SOD_123_611CB7E4_ln_077  label="D_24_2_D_SOD_123_611CB95A"
  LinkPlacement = pos=(11.176,28.2575,-1.6) rot=(0.707107,0.707107,0;3.14159rad)
  LinkedObject = -> Shape001
  Placement = pos=(11.176,28.2575,-1.6) rot=(0.707107,0.707107,0;3.14159rad)
FEATURE [App::Link] D_2_D_SOD_123_611CB7E4_ln_078  label="D_23_2_D_SOD_123_611CB949"
  LinkPlacement = pos=(-7.874,28.321,-1.6) rot=(0.707107,0.707107,0;3.14159rad)
  LinkedObject = -> Shape001
  Placement = pos=(-7.874,28.321,-1.6) rot=(0.707107,0.707107,0;3.14159rad)
FEATURE [App::Link] D_2_D_SOD_123_611CB7E4_ln_079  label="D_22_2_D_SOD_123_611CB938"
  LinkPlacement = pos=(-26.924,28.321,-1.6) rot=(0.707107,0.707107,0;3.14159rad)
  LinkedObject = -> Shape001
  Placement = pos=(-26.924,28.321,-1.6) rot=(0.707107,0.707107,0;3.14159rad)
FEATURE [App::Link] D_2_D_SOD_123_611CB7E4_ln_080  label="D_21_2_D_SOD_123_611CB927"
  LinkPlacement = pos=(-45.974,28.321,-1.6) rot=(0.707107,0.707107,0;3.14159rad)
  LinkedObject = -> Shape001
  Placement = pos=(-45.974,28.321,-1.6) rot=(0.707107,0.707107,0;3.14159rad)
FEATURE [App::Link] D_2_D_SOD_123_611CB7E4_ln_081  label="D_20_2_D_SOD_123_611CB916"
  LinkPlacement = pos=(-65.024,28.2575,-1.6) rot=(0.707107,0.707107,0;3.14159rad)
  LinkedObject = -> Shape001
  Placement = pos=(-65.024,28.2575,-1.6) rot=(0.707107,0.707107,0;3.14159rad)
FEATURE [App::Link] D_2_D_SOD_123_611CB7E4_ln_082  label="D_19_2_D_SOD_123_611CB905"
  LinkPlacement = pos=(-84.074,28.321,-1.6) rot=(0.707107,0.707107,0;3.14159rad)
  LinkedObject = -> Shape001
  Placement = pos=(-84.074,28.321,-1.6) rot=(0.707107,0.707107,0;3.14159rad)
FEATURE [App::Link] D_2_D_SOD_123_611CB7E4_ln_083  label="D_18_2_D_SOD_123_611CB8F4"
  LinkPlacement = pos=(-103.124,28.2575,-1.6) rot=(0.707107,0.707107,0;3.14159rad)
  LinkedObject = -> Shape001
  Placement = pos=(-103.124,28.2575,-1.6) rot=(0.707107,0.707107,0;3.14159rad)
FEATURE [App::Link] D_2_D_SOD_123_611CB7E4_ln_084  label="D_17_2_D_SOD_123_611CB8E3"
  LinkPlacement = pos=(-122.174,28.2575,-1.6) rot=(0.707107,0.707107,0;3.14159rad)
  LinkedObject = -> Shape001
  Placement = pos=(-122.174,28.2575,-1.6) rot=(0.707107,0.707107,0;3.14159rad)
FEATURE [App::Link] D_2_D_SOD_123_611CB7E4_ln_085  label="D_16_2_D_SOD_123_611CB8D2"
  LinkPlacement = pos=(128.524,47.371,-1.6) rot=(0.707107,0.707107,0;3.14159rad)
  LinkedObject = -> Shape001
  Placement = pos=(128.524,47.371,-1.6) rot=(0.707107,0.707107,0;3.14159rad)
FEATURE [App::Link] D_2_D_SOD_123_611CB7E4_ln_086  label="D_15_2_D_SOD_123_611CB8C1"
  LinkPlacement = pos=(125.476,47.371,-1.6) rot=(0.707107,0.707107,0;3.14159rad)
  LinkedObject = -> Shape001
  Placement = pos=(125.476,47.371,-1.6) rot=(0.707107,0.707107,0;3.14159rad)
FEATURE [App::Link] D_2_D_SOD_123_611CB7E4_ln_087  label="D_14_2_D_SOD_123_611CB8B0"
  LinkPlacement = pos=(106.426,47.371,-1.6) rot=(0.707107,0.707107,0;3.14159rad)
  LinkedObject = -> Shape001
  Placement = pos=(106.426,47.371,-1.6) rot=(0.707107,0.707107,0;3.14159rad)
FEATURE [App::Link] D_2_D_SOD_123_611CB7E4_ln_088  label="D_13_2_D_SOD_123_611CB89F"
  LinkPlacement = pos=(87.376,47.371,-1.6) rot=(0.707107,0.707107,0;3.14159rad)
  LinkedObject = -> Shape001
  Placement = pos=(87.376,47.371,-1.6) rot=(0.707107,0.707107,0;3.14159rad)
FEATURE [App::Link] D_2_D_SOD_123_611CB7E4_ln_089  label="D_12_2_D_SOD_123_611CB88E"
  LinkPlacement = pos=(68.326,47.371,-1.6) rot=(0.707107,0.707107,0;3.14159rad)
  LinkedObject = -> Shape001
  Placement = pos=(68.326,47.371,-1.6) rot=(0.707107,0.707107,0;3.14159rad)
FEATURE [App::Link] D_2_D_SOD_123_611CB7E4_ln_090  label="D_11_2_D_SOD_123_611CB87D"
  LinkPlacement = pos=(49.276,47.371,-1.6) rot=(0.707107,0.707107,0;3.14159rad)
  LinkedObject = -> Shape001
  Placement = pos=(49.276,47.371,-1.6) rot=(0.707107,0.707107,0;3.14159rad)
FEATURE [App::Link] D_2_D_SOD_123_611CB7E4_ln_091  label="D_10_2_D_SOD_123_611CB86C"
  LinkPlacement = pos=(30.226,47.371,-1.6) rot=(0.707107,0.707107,0;3.14159rad)
  LinkedObject = -> Shape001
  Placement = pos=(30.226,47.371,-1.6) rot=(0.707107,0.707107,0;3.14159rad)
FEATURE [App::Link] D_2_D_SOD_123_611CB7E4_ln_092  label="D_9_2_D_SOD_123_611CB85B"
  LinkPlacement = pos=(11.176,47.371,-1.6) rot=(0.707107,0.707107,0;3.14159rad)
  LinkedObject = -> Shape001
  Placement = pos=(11.176,47.371,-1.6) rot=(0.707107,0.707107,0;3.14159rad)
FEATURE [App::Link] D_2_D_SOD_123_611CB7E4_ln_093  label="D_8_2_D_SOD_123_611CB84A"
  LinkPlacement = pos=(-7.874,47.371,-1.6) rot=(0.707107,0.707107,0;3.14159rad)
  LinkedObject = -> Shape001
  Placement = pos=(-7.874,47.371,-1.6) rot=(0.707107,0.707107,0;3.14159rad)
FEATURE [App::Link] D_2_D_SOD_123_611CB7E4_ln_094  label="D_7_2_D_SOD_123_611CB839"
  LinkPlacement = pos=(-26.924,47.371,-1.6) rot=(0.707107,0.707107,0;3.14159rad)
  LinkedObject = -> Shape001
  Placement = pos=(-26.924,47.371,-1.6) rot=(0.707107,0.707107,0;3.14159rad)
FEATURE [App::Link] D_2_D_SOD_123_611CB7E4_ln_095  label="D_6_2_D_SOD_123_611CB828"
  LinkPlacement = pos=(-45.974,47.371,-1.6) rot=(0.707107,0.707107,0;3.14159rad)
  LinkedObject = -> Shape001
  Placement = pos=(-45.974,47.371,-1.6) rot=(0.707107,0.707107,0;3.14159rad)
FEATURE [App::Link] D_2_D_SOD_123_611CB7E4_ln_096  label="D_5_2_D_SOD_123_611CB817"
  LinkPlacement = pos=(-65.024,46.736,-1.6) rot=(0.707107,0.707107,0;3.14159rad)
  LinkedObject = -> Shape001
  Placement = pos=(-65.024,46.736,-1.6) rot=(0.707107,0.707107,0;3.14159rad)
FEATURE [App::Link] D_2_D_SOD_123_611CB7E4_ln_097  label="D_4_2_D_SOD_123_611CB806"
  LinkPlacement = pos=(-84.1375,47.371,-1.6) rot=(0.707107,0.707107,0;3.14159rad)
  LinkedObject = -> Shape001
  Placement = pos=(-84.1375,47.371,-1.6) rot=(0.707107,0.707107,0;3.14159rad)
FEATURE [App::Link] D_2_D_SOD_123_611CB7E4_ln_098  label="D_3_2_D_SOD_123_611CB7F5"
  LinkPlacement = pos=(-103.188,47.371,-1.6) rot=(0.707107,0.707107,0;3.14159rad)
  LinkedObject = -> Shape001
  Placement = pos=(-103.188,47.371,-1.6) rot=(0.707107,0.707107,0;3.14159rad)
FEATURE [App::Link] D_2_D_SOD_123_611CB7E4_ln_099  label="D26_2_D_SOD_123_611CB7C2"
  LinkPlacement = pos=(-136.112,17.7483,-1.6) rot=(0.707107,0.707107,0;3.14159rad)
  LinkedObject = -> Shape001
  Placement = pos=(-136.112,17.7483,-1.6) rot=(0.707107,0.707107,0;3.14159rad)
FEATURE [Part::Feature] Shape002  label="R7_R_0603_1608Metric_611CC01B[2]"
  Placement = pos=(-139.287,16.1607,-1.6) rot=(0,1,0;3.14159rad)
  shape: bbox 1.6 x 0.8 x 0.45 mm, 26 faces (baked)
FEATURE [App::Link] R7_R_0603_1608Metric_611CC01B_2__ln_  label="R6_R_0603_1608Metric_611CC011[2]"
  LinkPlacement = pos=(-158.178,36.5125,-1.6) rot=(0.707107,0.707107,0;3.14159rad)
  LinkedObject = -> Shape002
  Placement = pos=(-158.178,36.5125,-1.6) rot=(0.707107,0.707107,0;3.14159rad)
FEATURE [App::Link] R7_R_0603_1608Metric_611CC01B_2__ln_001  label="R4_R_0603_1608Metric_611CBFF6[2]"
  LinkPlacement = pos=(-144.463,24.6063,-1.6) rot=(1,0,0;3.14159rad)
  LinkedObject = -> Shape002
  Placement = pos=(-144.463,24.6063,-1.6) rot=(1,0,0;3.14159rad)
FEATURE [App::Link] R7_R_0603_1608Metric_611CC01B_2__ln_002  label="R3_R_0603_1608Metric_611CBFEC[2]"
  LinkPlacement = pos=(-144.463,26.1937,-1.6) rot=(0,1,0;3.14159rad)
  LinkedObject = -> Shape002
  Placement = pos=(-144.463,26.1937,-1.6) rot=(0,1,0;3.14159rad)
FEATURE [App::Link] R7_R_0603_1608Metric_611CC01B_2__ln_003  label="R2_R_0603_1608Metric_611CBFE2[2]"
  LinkPlacement = pos=(-95.758,38.0365,-1.6) rot=(-0.707107,0.707107,0;3.14159rad)
  LinkedObject = -> Shape002
  Placement = pos=(-95.758,38.0365,-1.6) rot=(-0.707107,0.707107,0;3.14159rad)
FEATURE [App::Link] R7_R_0603_1608Metric_611CC01B_2__ln_004  label="R1_R_0603_1608Metric_611CBFD8[2]"
  LinkPlacement = pos=(-98.425,35.3695,-1.6) rot=(0,1,0;3.14159rad)
  LinkedObject = -> Shape002
  Placement = pos=(-98.425,35.3695,-1.6) rot=(0,1,0;3.14159rad)
FEATURE [Part::Feature] Shape003  label="D3_LED_WS2812B_PLCC4_50x50mm_P32mm_611CB5AF"
  Placement = pos=(3.175,19.05,-1.6) rot=(0,1,0;3.14159rad)
  shape: bbox 5.4 x 5 x 1.6 mm, 68 faces (baked)
FEATURE [Part::Feature] Shape004  label="J1_(Unsaved)_611F973D"
  Placement = pos=(-165.556,28.575,-1.6) rot=(0.707107,0.707107,0;3.14159rad)
  shape: bbox 7.903 x 8.943 x 4.203 mm, 384 faces, 24 solids (baked)
FEATURE [Part::Feature] Shape005  label="Y1_Crystal_SMD_3225-4Pin_3.2x2.5mm_611CC0DE"
  Placement = pos=(-53.403,0.9525,-1.6) rot=(0.92388,0.382683,0;3.14159rad)
  shape: bbox 3.891 x 3.889 x 0.64 mm, 28 faces (baked)
FEATURE [Part::Feature] Shape006  label="U3_LQFP_64_10x10mm_P05mm_611CC0CC"
  Placement = pos=(-64.135,1.7145,-1.6) rot=(0,1,0;3.14159rad)
  shape: bbox 12 x 12 x 1.5 mm, 1004 faces (baked)
FEATURE [Part::Feature] Shape007  label="U2_SOT_23_6_611CC061"
  Placement = pos=(-157.162,28.575,-1.6) rot=(1,0,0;3.14159rad)
  shape: bbox 2.8 x 2.9 x 1.55 mm, 124 faces (baked)
FEATURE [Part::Feature] Shape008  label="U1_SOT_23_5_611CC04B"
  Placement = pos=(-82.55,19.05,-1.6) rot=(1,0,0;3.14159rad)
  shape: bbox 2.8 x 2.9 x 1.55 mm, 109 faces (baked)
FEATURE [Part::Feature] Shape009  label="SW1_EVQPUC02K_611CC036"
  Placement = pos=(-158.75,42.8625,-1.6) rot=(0.57735,0.57735,-0.57735;4.18879rad)
  shape: bbox 4.542 x 6.402 x 2.183 mm, 274 faces (baked)
FEATURE [App::Link] R7_R_0603_1608Metric_611CC01B_2__ln_005  label="R5_R_0603_1608Metric_611CC007"
  LinkPlacement = pos=(-73.279,3.3655,-1.6) rot=(0,1,0;3.14159rad)
  LinkedObject = -> Shape002
  Placement = pos=(-73.279,3.3655,-1.6) rot=(0,1,0;3.14159rad)
FEATURE [Part::Feature] Shape010  label="Q2_SOT_23_611CBFCE"
  Placement = pos=(-136.525,22.225,-1.6) rot=(0.707107,0.707107,0;3.14159rad)
  shape: bbox 3 x 2.5 x 1.2 mm, 76 faces (baked)
FEATURE [App::Link] Q2_SOT_23_611CBFCE_ln_  label="Q1_SOT_23_611CBFB9"
  LinkPlacement = pos=(-98.425,38.1,-1.6) rot=(0,1,0;3.14159rad)
  LinkedObject = -> Shape010
  Placement = pos=(-98.425,38.1,-1.6) rot=(0,1,0;3.14159rad)
FEATURE [Part::Feature] Shape011  label="J2_PinHeader_1x06_P254mm_Vertical_611CBEB1"
  Placement = pos=(-139.7,32.5437,-1.6) rot=(0,1,0;3.14159rad)
  shape: bbox 2.54 x 15.24 x 11.54 mm, 148 faces (baked)
FEATURE [Part::Feature] Shape012  label="F1_User Library-ptc06032-1_611CBE77"
  Placement = pos=(-144.319,33.3375,-1.6) rot=(0,1,0;3.14159rad)
  shape: bbox 1.6 x 0.75 x 0.755 mm, 42 faces (baked)
FEATURE [Part::Feature] Shape013  label="D25_LED_0603_1608Metric_611CB7B1"
  Placement = pos=(-159.829,36.5125,-1.6) rot=(0.707107,0.707107,0;3.14159rad)
  shape: bbox 0.8 x 1.6 x 1.1 mm, 50 faces (baked)
FEATURE [App::Link] D3_LED_WS2812B_PLCC4_50x50mm_P32mm_611CB5AF_ln_  label="D20_LED_WS2812B_PLCC4_50x50mm_P32mm_611CB736"
  LinkPlacement = pos=(-101.6,-38.0995,-1.6) rot=(0,1,0;3.14159rad)
  LinkedObject = -> Shape003
  Placement = pos=(-101.6,-38.0995,-1.6) rot=(0,1,0;3.14159rad)
FEATURE [App::Link] D3_LED_WS2812B_PLCC4_50x50mm_P32mm_611CB5AF_ln_001  label="D19_LED_WS2812B_PLCC4_50x50mm_P32mm_611CB71F"
  LinkPlacement = pos=(-44.577,-38.0995,-1.6) rot=(0,1,0;3.14159rad)
  LinkedObject = -> Shape003
  Placement = pos=(-44.577,-38.0995,-1.6) rot=(0,1,0;3.14159rad)
FEATURE [App::Link] D3_LED_WS2812B_PLCC4_50x50mm_P32mm_611CB5AF_ln_002  label="D18_LED_WS2812B_PLCC4_50x50mm_P32mm_611CB708"
  LinkPlacement = pos=(3.175,-38.0995,-1.6) rot=(0,1,0;3.14159rad)
  LinkedObject = -> Shape003
  Placement = pos=(3.175,-38.0995,-1.6) rot=(0,1,0;3.14159rad)
FEATURE [App::Link] D3_LED_WS2812B_PLCC4_50x50mm_P32mm_611CB5AF_ln_003  label="D17_LED_WS2812B_PLCC4_50x50mm_P32mm_611CB6F1"
  LinkPlacement = pos=(69.799,-38.1245,-1.6) rot=(0,1,0;3.14159rad)
  LinkedObject = -> Shape003
  Placement = pos=(69.799,-38.1245,-1.6) rot=(0,1,0;3.14159rad)
FEATURE [App::Link] D3_LED_WS2812B_PLCC4_50x50mm_P32mm_611CB5AF_ln_004  label="D16_LED_WS2812B_PLCC4_50x50mm_P32mm_611CB6DA"
  LinkPlacement = pos=(127,-38.0995,-1.6) rot=(0,1,0;3.14159rad)
  LinkedObject = -> Shape003
  Placement = pos=(127,-38.0995,-1.6) rot=(0,1,0;3.14159rad)
FEATURE [App::Link] D3_LED_WS2812B_PLCC4_50x50mm_P32mm_611CB5AF_ln_005  label="D15_LED_WS2812B_PLCC4_50x50mm_P32mm_611CB6C3"
  LinkPlacement = pos=(127,-19.0495,-1.6) rot=(0,1,0;3.14159rad)
  LinkedObject = -> Shape003
  Placement = pos=(127,-19.0495,-1.6) rot=(0,1,0;3.14159rad)
FEATURE [App::Link] D3_LED_WS2812B_PLCC4_50x50mm_P32mm_611CB5AF_ln_006  label="D14_LED_WS2812B_PLCC4_50x50mm_P32mm_611CB6AC"
  LinkPlacement = pos=(69.85,-19.0495,-1.6) rot=(0,1,0;3.14159rad)
  LinkedObject = -> Shape003
  Placement = pos=(69.85,-19.0495,-1.6) rot=(0,1,0;3.14159rad)
FEATURE [App::Link] D3_LED_WS2812B_PLCC4_50x50mm_P32mm_611CB5AF_ln_007  label="D13_LED_WS2812B_PLCC4_50x50mm_P32mm_611CB695"
  LinkPlacement = pos=(3.175,-19.0495,-1.6) rot=(0,1,0;3.14159rad)
  LinkedObject = -> Shape003
  Placement = pos=(3.175,-19.0495,-1.6) rot=(0,1,0;3.14159rad)
FEATURE [App::Link] D3_LED_WS2812B_PLCC4_50x50mm_P32mm_611CB5AF_ln_008  label="D12_LED_WS2812B_PLCC4_50x50mm_P32mm_611CB67E"
  LinkPlacement = pos=(-44.45,-19.0495,-1.6) rot=(0,1,0;3.14159rad)
  LinkedObject = -> Shape003
  Placement = pos=(-44.45,-19.0495,-1.6) rot=(0,1,0;3.14159rad)
FEATURE [App::Link] D3_LED_WS2812B_PLCC4_50x50mm_P32mm_611CB5AF_ln_009  label="D11_LED_WS2812B_PLCC4_50x50mm_P32mm_611CB667"
  LinkPlacement = pos=(-101.6,-19.0495,-1.6) rot=(0,1,0;3.14159rad)
  LinkedObject = -> Shape003
  Placement = pos=(-101.6,-19.0495,-1.6) rot=(0,1,0;3.14159rad)
FEATURE [App::Link] D3_LED_WS2812B_PLCC4_50x50mm_P32mm_611CB5AF_ln_010  label="D10_LED_WS2812B_PLCC4_50x50mm_P32mm_611CB650"
  LinkPlacement = pos=(-101.6,0,-1.6) rot=(0,1,0;3.14159rad)
  LinkedObject = -> Shape003
  Placement = pos=(-101.6,0,-1.6) rot=(0,1,0;3.14159rad)
FEATURE [App::Link] D3_LED_WS2812B_PLCC4_50x50mm_P32mm_611CB5AF_ln_011  label="D9_LED_WS2812B_PLCC4_50x50mm_P32mm_611CB639"
  LinkPlacement = pos=(-44.45,0,-1.6) rot=(0,1,0;3.14159rad)
  LinkedObject = -> Shape003
  Placement = pos=(-44.45,0,-1.6) rot=(0,1,0;3.14159rad)
FEATURE [App::Link] D3_LED_WS2812B_PLCC4_50x50mm_P32mm_611CB5AF_ln_012  label="D8_LED_WS2812B_PLCC4_50x50mm_P32mm_611CB622"
  LinkPlacement = pos=(3.175,0,-1.6) rot=(0,1,0;3.14159rad)
  LinkedObject = -> Shape003
  Placement = pos=(3.175,0,-1.6) rot=(0,1,0;3.14159rad)
FEATURE [App::Link] D3_LED_WS2812B_PLCC4_50x50mm_P32mm_611CB5AF_ln_013  label="D7_LED_WS2812B_PLCC4_50x50mm_P32mm_611CB60B"
  LinkPlacement = pos=(69.85,0,-1.6) rot=(0,1,0;3.14159rad)
  LinkedObject = -> Shape003
  Placement = pos=(69.85,0,-1.6) rot=(0,1,0;3.14159rad)
FEATURE [App::Link] D3_LED_WS2812B_PLCC4_50x50mm_P32mm_611CB5AF_ln_014  label="D6_LED_WS2812B_PLCC4_50x50mm_P32mm_611CB5F4"
  LinkPlacement = pos=(127,0,-1.6) rot=(0,1,0;3.14159rad)
  LinkedObject = -> Shape003
  Placement = pos=(127,0,-1.6) rot=(0,1,0;3.14159rad)
FEATURE [App::Link] D3_LED_WS2812B_PLCC4_50x50mm_P32mm_611CB5AF_ln_015  label="D5_LED_WS2812B_PLCC4_50x50mm_P32mm_611CB5DD"
  LinkPlacement = pos=(127,19.05,-1.6) rot=(0,1,0;3.14159rad)
  LinkedObject = -> Shape003
  Placement = pos=(127,19.05,-1.6) rot=(0,1,0;3.14159rad)
FEATURE [App::Link] D3_LED_WS2812B_PLCC4_50x50mm_P32mm_611CB5AF_ln_016  label="D4_LED_WS2812B_PLCC4_50x50mm_P32mm_611CB5C6"
  LinkPlacement = pos=(69.85,19.05,-1.6) rot=(0,1,0;3.14159rad)
  LinkedObject = -> Shape003
  Placement = pos=(69.85,19.05,-1.6) rot=(0,1,0;3.14159rad)
FEATURE [App::Link] D3_LED_WS2812B_PLCC4_50x50mm_P32mm_611CB5AF_ln_017  label="D2_LED_WS2812B_PLCC4_50x50mm_P32mm_611E9F10"
  LinkPlacement = pos=(-44.45,19.05,-1.6) rot=(0,1,0;3.14159rad)
  LinkedObject = -> Shape003
  Placement = pos=(-44.45,19.05,-1.6) rot=(0,1,0;3.14159rad)
FEATURE [App::Link] D3_LED_WS2812B_PLCC4_50x50mm_P32mm_611CB5AF_ln_018  label="D1_LED_WS2812B_PLCC4_50x50mm_P32mm_611CB581"
  LinkPlacement = pos=(-101.6,19.05,-1.6) rot=(0,1,0;3.14159rad)
  LinkedObject = -> Shape003
  Placement = pos=(-101.6,19.05,-1.6) rot=(0,1,0;3.14159rad)
FEATURE [Part::Feature] Shape014  label="BZ1_Buzzer_Murata_PKMCS0909E4000_R1_611CB3F8"
  Placement = pos=(-23.019,0,-1.6) rot=(1,0,0;3.14159rad)
  shape: bbox 9 x 9 x 1.9 mm, 41 faces (baked)
FEATURE [App::Part] Bot_e1db
  Group = -> [Shape,C37_C_0603_1608Metric_611CB56A_ln_,C37_C_0603_1608Metric_611CB56A_ln_001,C37_C_0603_1608Metric_611CB56A_ln_002,C37_C_0603_1608Metric_611CB56A_ln_003,C37_C_0603_1608Metric_611CB56A_ln_004,C37_C_0603_1608Metric_611CB56A_ln_005,C37_C_0603_1608Metric_611CB56A_ln_006,C37_C_0603_1608Metric_611CB56A_ln_007,C37_C_0603_1608Metric_611CB56A_ln_008,C37_C_0603_1608Metric_611CB56A_ln_009,+166 more]
  Origin = -> Origin004
FEATURE [App::Part] Step_Models_e1db
  Group = -> [Bot_e1db]
  Origin = -> Origin002
FEATURE [Part::Feature] topTracks_e1db
  Placement = pos=(-174.625,80.9625,0.01) rot=(0,0,1;0rad)
  shape: bbox 335.5 x 119.6 x 0.04 mm, 416 faces, 0 solids (baked)
FEATURE [Part::Feature] botTracks_e1db
  Placement = pos=(-174.625,80.9625,-1.61) rot=(0,0,1;0rad)
  shape: bbox 335.5 x 119.6 x 0.04 mm, 1331 faces, 0 solids (baked)
FEATURE [App::Part] Board_Geoms_e1db
  Group = -> [Local_CS_e1db,Pcb_e1db,PCB_Sketch_e1db,topTracks_e1db,botTracks_e1db]
  Origin = -> Origin
FEATURE [App::Part] Board_e1db  label="Orthonite87_PCB"
  Group = -> [Board_Geoms_e1db,Step_Models_e1db]
  Origin = -> Origin001
